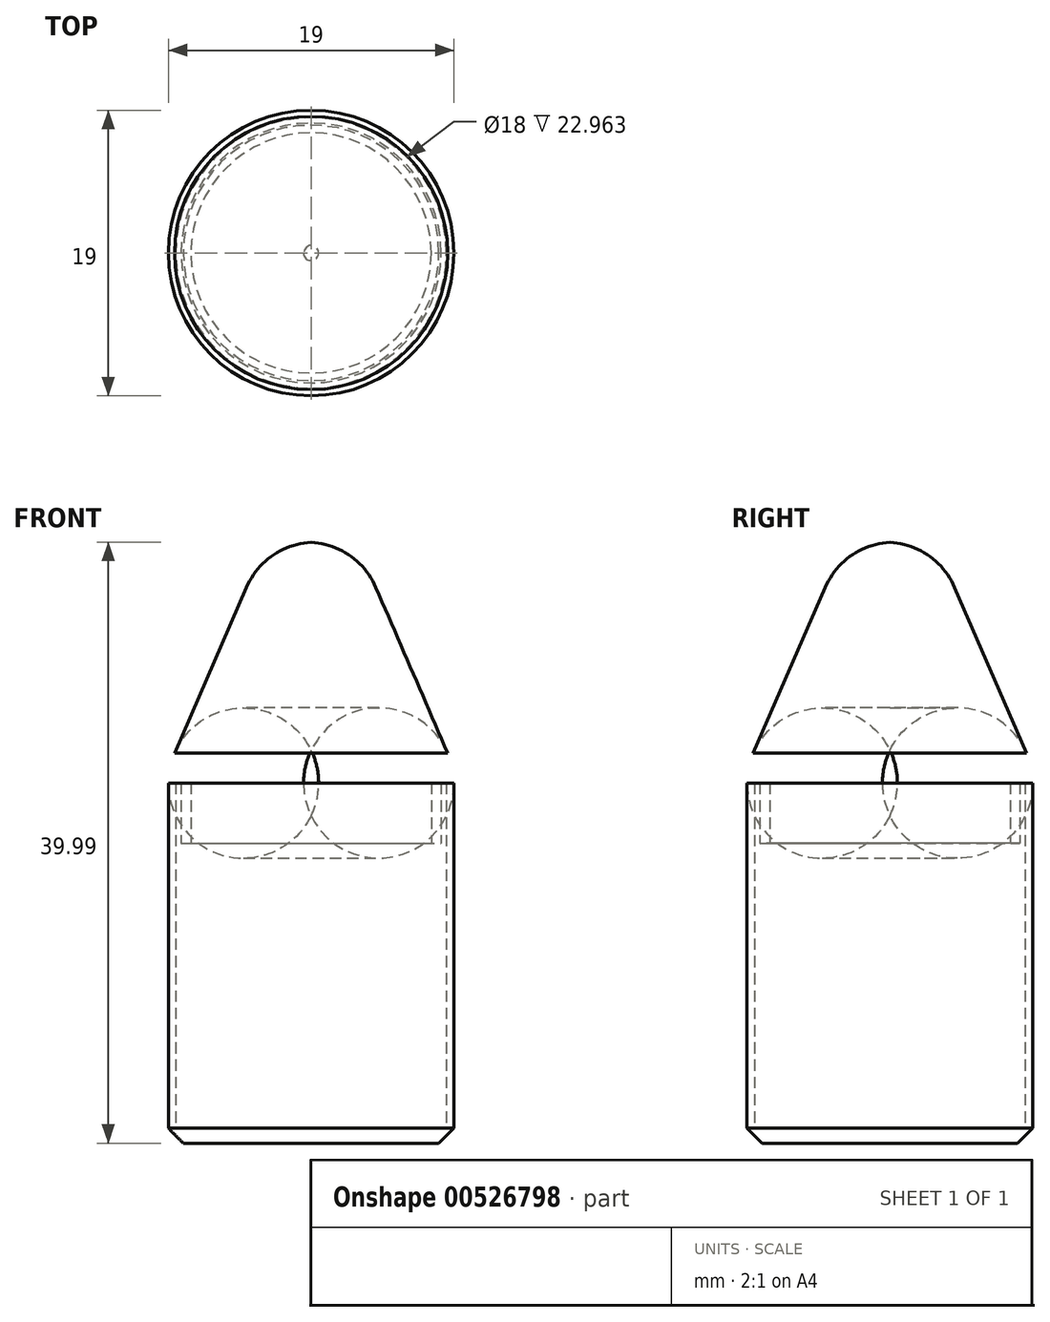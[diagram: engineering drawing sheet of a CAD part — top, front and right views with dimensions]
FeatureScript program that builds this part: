
annotation { "Feature Type Name" : "Feature", "Feature Type Description" : "" }
export const myFeature = defineFeature(function(context is Context, id is Id, definition is map)
    precondition{}
    {
        {
            var Q0;
            Q0=qCreatedBy(makeId("Front.planeOp"),FACE);
            var sketch = newSketch(context, id + "F0", { "sketchPlane" : qUnion([Q0])});
            skLineSegment(sketch, "E0.bottom", {"start": v(0, 0) * mm, "end": v(-9.5, 0) * mm});
            skLineSegment(sketch, "E0.left", {"start": v(0, 0) * mm, "end": v(0, 15) * mm});
            skLineSegment(sketch, "E0.right", {"start": v(-9.5, 0) * mm, "end": v(-9.5, 23.96) * mm});
            skLineSegment(sketch, "E1.top", {"start": v(-9.5, 40) * mm, "end": v(0, 40) * mm, "construction": true});
            skLineSegment(sketch, "E1.left", {"start": v(-9.5, 25) * mm, "end": v(-9.5, 40) * mm, "construction": true});
            skLineSegment(sketch, "E1.right", {"start": v(0, 15) * mm, "end": v(0, 40) * mm, "construction": true});
            skLineSegment(sketch, "E2", {"start": v(-9.09, 25.95) * mm, "end": v(-4.3, 36.99) * mm});
            skLineSegment(sketch, "E3", {"start": v(0, 40) * mm, "end": v(0.28, 40) * mm});
            skLineSegment(sketch, "E4", {"start": v(0, 40) * mm, "end": v(0, 15) * mm});
            skPoint(sketch, "E5.visualSharp", {"position": v(-9.5, 25) * mm});
            skArc(sketch, "E5.filletArc", {"start": v(-9.09, 25.95) * mm, "mid": v(-9.4, 24.98) * mm, "end": v(-9.5, 23.96) * mm});
            skPoint(sketch, "E6.visualSharp", {"position": v(-3, 40) * mm});
            skArc(sketch, "E6.filletArc", {"start": v(0.28, 40) * mm, "mid": v(-2.46, 39.18) * mm, "end": v(-4.3, 36.99) * mm});
            skLineSegment(sketch, "E7", {"start": v(-9, 1) * mm, "end": v(-9, 23.96) * mm});
            skLineSegment(sketch, "E8", {"start": v(-9.5, 23.96) * mm, "end": v(-9, 23.96) * mm, "construction": true});
            skLineSegment(sketch, "E9", {"start": v(-9, 23.96) * mm, "end": v(0, 23.96) * mm});
            skLineSegment(sketch, "E10", {"start": v(-9, 1) * mm, "end": v(0, 1) * mm});
            skLineSegment(sketch, "E11", {"start": v(-9.5, 23.96) * mm, "end": v(-9, 23.96) * mm});
            skSolve(sketch);
        }
        {
            var Q0;
            {var subQ1=sQuery(id+"F0.wireOp",EDGE,"E0.bottom");Q0=makeQuery(id+"F0.imprint","IMPRINT",FACE,{"disambiguationData":[TD([[makeQuery(id+"F0.imprint","IMPRINT",EDGE,{"derivedFrom":subQ1}),-1.0]])]});}
            var Q1;
            Q1=sQuery(id+"F0.wireOp",EDGE,"E0.left");
            revolve(context, id + "F1", {"entities" : qUnion([Q0]), "axis" : qUnion([Q1]), "revolveType" : RevolveType.FULL});
        }
        {
            var Q0;
            Q0=makeQuery(id+"F0.imprint","IMPRINT",FACE,{"disambiguationData":[TD([[makeQuery(id+"F0.imprint","IMPRINT",EDGE,{"derivedFrom":sQuery(id+"F0.wireOp",EDGE,"E2")}),-1.0]])]});
            var sketch = newSketch(context, id + "F2", { "sketchPlane" : qUnion([Q0])});
            skLineSegment(sketch, "E12", {"start": v(-8.65, 23.96) * mm, "end": v(-8.65, 19.96) * mm});
            skLineSegment(sketch, "E13", {"start": v(-8.65, 19.96) * mm, "end": v(-8, 19.96) * mm});
            skLineSegment(sketch, "E14", {"start": v(-8, 19.96) * mm, "end": v(-8, 23.96) * mm});
            skLineSegment(sketch, "E15", {"start": v(-8.65, 23.96) * mm, "end": v(-8, 23.96) * mm, "construction": true});
            skLineSegment(sketch, "E16", {"start": v(-8.65, 23.96) * mm, "end": v(-8, 23.96) * mm});
            skSolve(sketch);
        }
        {
            var Q0;
            Q0=makeQuery(id+"F0.imprint","IMPRINT",FACE,{"disambiguationData":[TD([[makeQuery(id+"F0.imprint","IMPRINT",EDGE,{"derivedFrom":sQuery(id+"F0.wireOp",EDGE,"E2")}),-1.0]])]});
            var Q1;
            Q1=sQuery(id+"F0.wireOp",EDGE,"E4");
            revolve(context, id + "F3", {"entities" : qUnion([Q0]), "axis" : qUnion([Q1]), "revolveType" : RevolveType.FULL});
        }
        {
            var Q0;
            Q0=makeQuery(id+"F2.imprint","IMPRINT",FACE,{"disambiguationData":[TD([[makeQuery(id+"F2.imprint","IMPRINT",EDGE,{"derivedFrom":sQuery(id+"F2.wireOp",EDGE,"E12")}),1.0]])]});
            var Q1;
            Q1=sQuery(id+"F0.wireOp",EDGE,"E0.left");
            revolve(context, id + "F4", {"operationType" : NewBodyOperationType.ADD, "entities" : qUnion([Q0]), "axis" : qUnion([Q1]), "revolveType" : RevolveType.FULL});
        }
        {
            var Q0;
            Q0=makeQuery(id+"F1.opRevolve","SWEPT_EDGE",EDGE,{"disambiguationData":[OSD([sQuery(id+"F0.wireOp",EDGE,"E0.bottom"),sQuery(id+"F0.wireOp",EDGE,"E0.right")])]});
            chamfer(context, id + "F5", {"entities" : qUnion([Q0]), "width" : 1 * mm, "tangentPropagation" : true});
        }
    });
